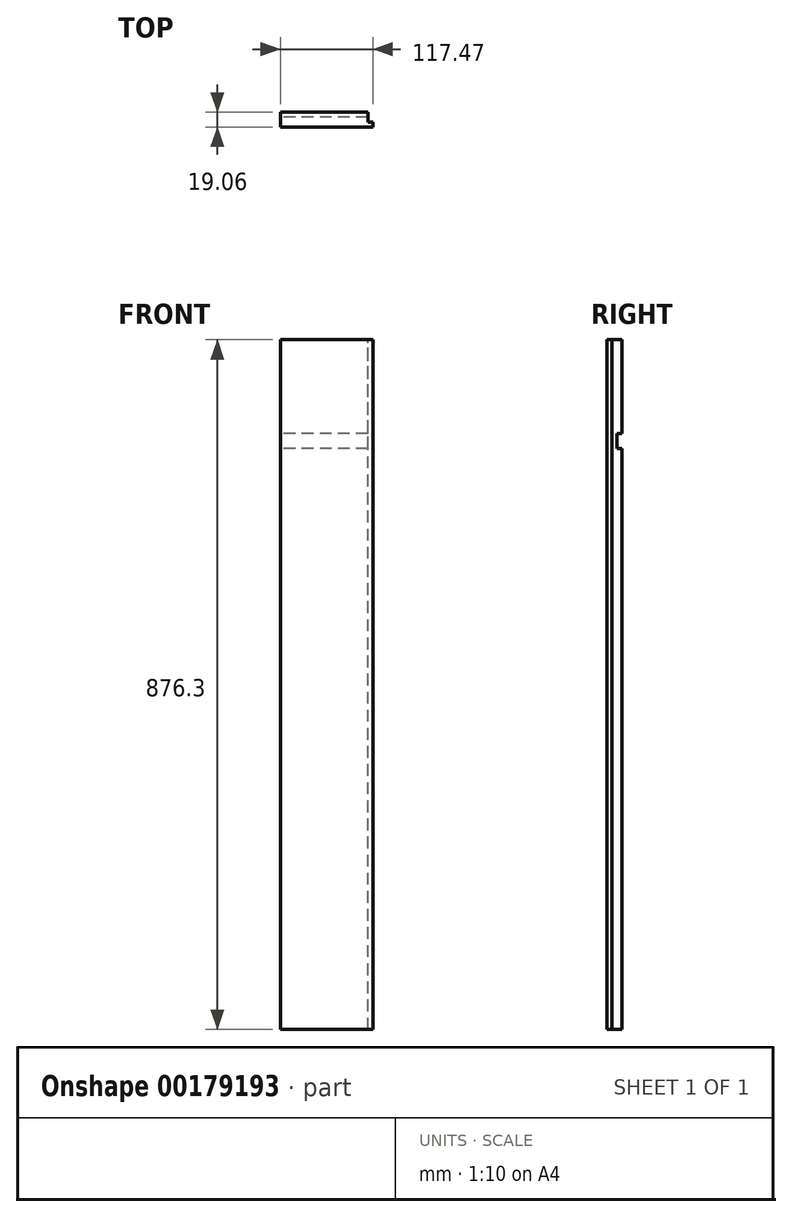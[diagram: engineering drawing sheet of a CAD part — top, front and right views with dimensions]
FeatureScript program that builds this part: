
annotation { "Feature Type Name" : "Feature", "Feature Type Description" : "" }
export const myFeature = defineFeature(function(context is Context, id is Id, definition is map)
    precondition{}
    {
        {
            var Q0;
            Q0=qCreatedBy(makeId("Front.planeOp"),FACE);
            var sketch = newSketch(context, id + "F0", { "sketchPlane" : qUnion([Q0])});
            skLineSegment(sketch, "E0.bottom", {"start": v(-247.9, 438.15) * mm, "end": v(-130.43, 438.15) * mm});
            skLineSegment(sketch, "E0.top", {"start": v(-247.9, -438.15) * mm, "end": v(-130.43, -438.15) * mm});
            skLineSegment(sketch, "E0.left", {"start": v(-247.9, 438.15) * mm, "end": v(-247.9, -438.15) * mm});
            skLineSegment(sketch, "E0.right", {"start": v(-130.43, 438.15) * mm, "end": v(-130.43, -438.15) * mm});
            skLineSegment(sketch, "E1", {"start": v(-247.9, 0) * mm, "end": v(-130.43, 0) * mm});
            skSolve(sketch);
        }
        {
            var Q0;
            {var subQ0=sQuery(id+"F0.wireOp",EDGE,"E0.bottom");Q0=makeQuery(id+"F0.imprint","IMPRINT",FACE,{"disambiguationData":[TD([[makeQuery(id+"F0.imprint","IMPRINT",EDGE,{"derivedFrom":subQ0}),-1.0]])]});}
            var Q1;
            {var subQ0=sQuery(id+"F0.wireOp",EDGE,"E0.top");Q1=makeQuery(id+"F0.imprint","IMPRINT",FACE,{"disambiguationData":[TD([[makeQuery(id+"F0.imprint","IMPRINT",EDGE,{"derivedFrom":subQ0}),1.0]])]});}
            extrude(context, id + "F1", {"entities" : qUnion([Q0, Q1]), "depth" : 19.05 * mm, "symmetric" : true});
        }
        {
            var Q0;
            Q0=makeQuery(id+"F1.opExtrude","CAP_FACE",FACE,{"disambiguationData":[OSD([sQuery(id+"F0.wireOp",EDGE,"E0.bottom"),sQuery(id+"F0.wireOp",EDGE,"E0.top"),sQuery(id+"F0.wireOp",EDGE,"E0.left"),sQuery(id+"F0.wireOp",EDGE,"E0.right")])],"isStart":true});
            var sketch = newSketch(context, id + "F2", { "sketchPlane" : qUnion([Q0])});
            skLineSegment(sketch, "E2.bottom", {"start": v(130.43, 300.04) * mm, "end": v(247.9, 300.04) * mm});
            skLineSegment(sketch, "E2.top", {"start": v(130.43, 319.09) * mm, "end": v(247.9, 319.09) * mm});
            skLineSegment(sketch, "E2.left", {"start": v(130.43, 300.04) * mm, "end": v(130.43, 319.09) * mm});
            skLineSegment(sketch, "E2.right", {"start": v(247.9, 300.04) * mm, "end": v(247.9, 319.09) * mm});
            skSolve(sketch);
        }
        {
            var Q0;
            Q0=makeQuery(id+"F2.imprint","IMPRINT",FACE,{"disambiguationData":[TD([[makeQuery(id+"F2.imprint","IMPRINT",EDGE,{"derivedFrom":sQuery(id+"F2.wireOp",EDGE,"E2.bottom")}),1.0]])]});
            extrude(context, id + "F3", {"entities" : qUnion([Q0]), "operationType" : NewBodyOperationType.REMOVE, "oppositeDirection" : true, "depth" : 6.35 * mm});
        }
        {
            var Q0;
            {var subQ0=sQuery(id+"F0.wireOp",EDGE,"E0.top");var subQ1=sQuery(id+"F0.wireOp",EDGE,"E0.left");var subQ2=sQuery(id+"F0.wireOp",EDGE,"E0.right");Q0=makeQuery(id+"F3.boolean.opBoolean","SPLIT",FACE,{"disambiguationData":[TD([makeQuery(id+"F1.opExtrude","SWEPT_FACE",FACE,{"disambiguationData":[OSD([subQ0])]})])],"derivedFrom":makeQuery(id+"F1.opExtrude","CAP_FACE",FACE,{"disambiguationData":[OSD([sQuery(id+"F0.wireOp",EDGE,"E0.bottom"),subQ0,subQ1,subQ2])],"isStart":true})});}
            var sketch = newSketch(context, id + "F4", { "sketchPlane" : qUnion([Q0])});
            skLineSegment(sketch, "E3.bottom", {"start": v(130.43, -438.15) * mm, "end": v(136.78, -438.15) * mm});
            skLineSegment(sketch, "E3.top", {"start": v(130.43, 438.15) * mm, "end": v(136.78, 438.15) * mm});
            skLineSegment(sketch, "E3.left", {"start": v(130.43, -438.15) * mm, "end": v(130.43, 438.15) * mm});
            skLineSegment(sketch, "E3.right", {"start": v(136.78, -438.15) * mm, "end": v(136.78, 438.15) * mm});
            skSolve(sketch);
        }
        {
            var Q0;
            {var subQ0=sQuery(id+"F4.wireOp",EDGE,"E3.top");Q0=makeQuery(id+"F4.imprint","IMPRINT",FACE,{"disambiguationData":[TD([[makeQuery(id+"F4.imprint","IMPRINT",EDGE,{"derivedFrom":subQ0}),-1.0]])]});}
            var Q1;
            {var subQ0=sQuery(id+"F4.wireOp",EDGE,"E3.bottom");Q1=makeQuery(id+"F4.imprint","IMPRINT",FACE,{"disambiguationData":[TD([[makeQuery(id+"F4.imprint","IMPRINT",EDGE,{"derivedFrom":subQ0}),-1.0]])]});}
            extrude(context, id + "F5", {"entities" : qUnion([Q0, Q1]), "operationType" : NewBodyOperationType.REMOVE, "oppositeDirection" : true, "depth" : 12.7 * mm});
        }
    });
